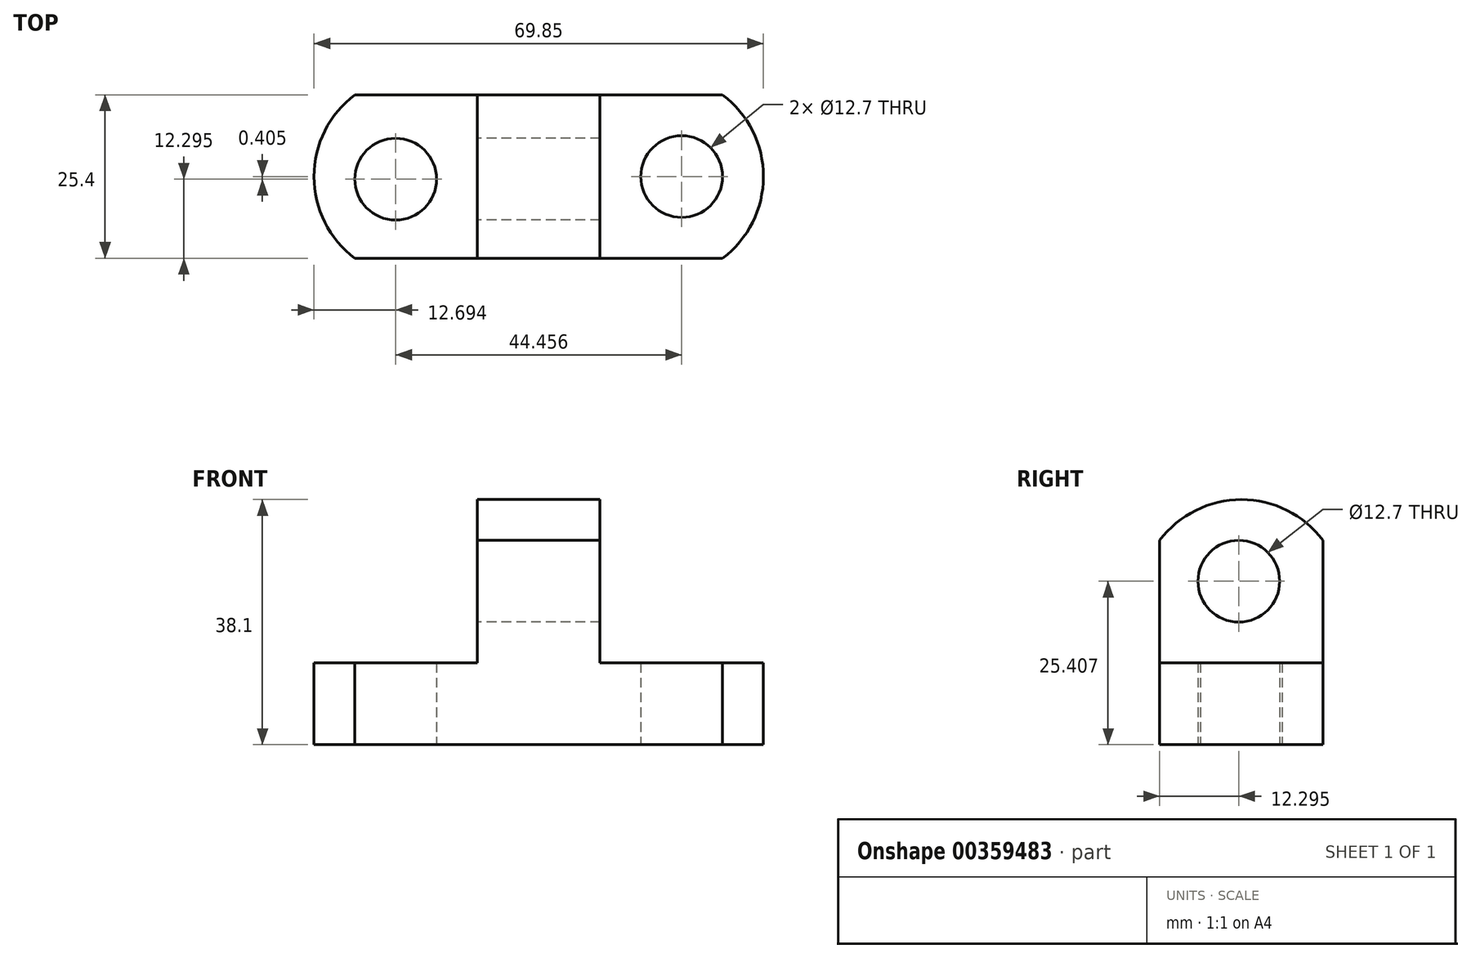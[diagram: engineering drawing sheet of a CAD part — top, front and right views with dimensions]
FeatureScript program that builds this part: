
annotation { "Feature Type Name" : "Feature", "Feature Type Description" : "" }
export const myFeature = defineFeature(function(context is Context, id is Id, definition is map)
    precondition{}
    {
        {
            var Q0;
            Q0=qCreatedBy(makeId("Front.planeOp"),FACE);
            var sketch = newSketch(context, id + "F0", { "sketchPlane" : qUnion([Q0])});
            skLineSegment(sketch, "E0", {"start": v(0, 38.1) * mm, "end": v(0, 0) * mm});
            skLineSegment(sketch, "E1", {"start": v(0, 0) * mm, "end": v(69.85, 0) * mm});
            skLineSegment(sketch, "E2", {"start": v(69.85, 0) * mm, "end": v(69.85, 38.1) * mm});
            skLineSegment(sketch, "E3", {"start": v(69.85, 38.1) * mm, "end": v(0, 38.1) * mm});
            skSolve(sketch);
        }
        {
            var Q0;
            Q0 = qSketchRegion(id + "F0", true);
            extrude(context, id + "F1", {"entities" : qUnion([Q0]), "oppositeDirection" : true, "depth" : 25.4 * mm});
        }
        {
            var Q0;
            Q0=qCreatedBy(makeId("Front.planeOp"),FACE);
            var sketch = newSketch(context, id + "F2", { "sketchPlane" : qUnion([Q0])});
            skLineSegment(sketch, "E4", {"start": v(44.45, 38.1) * mm, "end": v(44.45, 12.7) * mm});
            skLineSegment(sketch, "E5", {"start": v(44.45, 12.7) * mm, "end": v(69.85, 12.7) * mm});
            skLineSegment(sketch, "E6", {"start": v(69.85, 12.7) * mm, "end": v(69.85, 38.1) * mm});
            skLineSegment(sketch, "E7", {"start": v(69.85, 38.1) * mm, "end": v(44.45, 38.1) * mm});
            skSolve(sketch);
        }
        {
            var Q0;
            Q0 = qSketchRegion(id + "F2", true);
            extrude(context, id + "F3", {"entities" : qUnion([Q0]), "operationType" : NewBodyOperationType.REMOVE, "oppositeDirection" : true, "depth" : 25.4 * mm});
        }
        {
            var Q0;
            Q0=qCreatedBy(makeId("Front.planeOp"),FACE);
            var sketch = newSketch(context, id + "F4", { "sketchPlane" : qUnion([Q0])});
            skLineSegment(sketch, "E8", {"start": v(25.4, 38.1) * mm, "end": v(25.4, 12.7) * mm});
            skLineSegment(sketch, "E9", {"start": v(25.4, 12.7) * mm, "end": v(0, 12.7) * mm});
            skLineSegment(sketch, "E10", {"start": v(0, 12.7) * mm, "end": v(0, 38.1) * mm});
            skLineSegment(sketch, "E11", {"start": v(0, 38.1) * mm, "end": v(25.4, 38.1) * mm});
            skSolve(sketch);
        }
        {
            var Q0;
            Q0 = qSketchRegion(id + "F4", true);
            extrude(context, id + "F5", {"entities" : qUnion([Q0]), "operationType" : NewBodyOperationType.REMOVE, "oppositeDirection" : true, "depth" : 25.4 * mm});
        }
        {
            var Q0;
            Q0=qCreatedBy(makeId("Top.planeOp"),FACE);
            var sketch = newSketch(context, id + "F6", { "sketchPlane" : qUnion([Q0])});
            skArc(sketch, "E12", {"start": v(63.5, 0) * mm, "mid": v(69.85, 12.7) * mm, "end": v(63.5, 25.4) * mm});
            skLineSegment(sketch, "E13", {"start": v(63.5, 25.4) * mm, "end": v(69.85, 25.4) * mm});
            skLineSegment(sketch, "E14", {"start": v(69.85, 25.4) * mm, "end": v(69.85, 0) * mm});
            skLineSegment(sketch, "E15", {"start": v(69.85, 0) * mm, "end": v(63.5, 0) * mm});
            skSolve(sketch);
        }
        {
            var Q0;
            Q0 = qSketchRegion(id + "F6", true);
            extrude(context, id + "F7", {"entities" : qUnion([Q0]), "operationType" : NewBodyOperationType.REMOVE, "depth" : 25.4 * mm});
        }
        {
            var Q0;
            Q0=qCreatedBy(makeId("Top.planeOp"),FACE);
            var sketch = newSketch(context, id + "F8", { "sketchPlane" : qUnion([Q0])});
            skArc(sketch, "E16", {"start": v(6.35, 25.4) * mm, "mid": v(0, 12.7) * mm, "end": v(6.35, 0) * mm});
            skLineSegment(sketch, "E17", {"start": v(6.35, 25.4) * mm, "end": v(0, 25.4) * mm});
            skLineSegment(sketch, "E18", {"start": v(0, 25.4) * mm, "end": v(0, 0) * mm});
            skLineSegment(sketch, "E19", {"start": v(0, 0) * mm, "end": v(6.35, 0) * mm});
            skSolve(sketch);
        }
        {
            var Q0;
            Q0 = qSketchRegion(id + "F8", true);
            extrude(context, id + "F9", {"entities" : qUnion([Q0]), "operationType" : NewBodyOperationType.REMOVE, "depth" : 25.4 * mm});
        }
        {
            var Q0;
            Q0=qCreatedBy(makeId("Right.planeOp"),FACE);
            var sketch = newSketch(context, id + "F10", { "sketchPlane" : qUnion([Q0])});
            skArc(sketch, "E20", {"start": v(25.4, 31.75) * mm, "mid": v(12.7, 38.1) * mm, "end": v(0, 31.75) * mm});
            skLineSegment(sketch, "E21", {"start": v(0, 31.75) * mm, "end": v(0, 38.1) * mm});
            skLineSegment(sketch, "E22", {"start": v(0, 38.1) * mm, "end": v(25.4, 38.1) * mm});
            skLineSegment(sketch, "E23", {"start": v(25.4, 38.1) * mm, "end": v(25.4, 31.75) * mm});
            skSolve(sketch);
        }
        {
            var Q0;
            Q0 = qSketchRegion(id + "F10", true);
            extrude(context, id + "F11", {"entities" : qUnion([Q0]), "operationType" : NewBodyOperationType.REMOVE, "depth" : 50.8 * mm});
        }
        {
            var Q0;
            Q0=qCreatedBy(makeId("Top.planeOp"),FACE);
            var sketch = newSketch(context, id + "F12", { "sketchPlane" : qUnion([Q0])});
            skCircle(sketch, "E24", {"center": v(12.7, 12.3) * mm, "radius": 6.35 * mm});
            skCircle(sketch, "E25", {"center": v(57.15, 12.7) * mm, "radius": 6.35 * mm});
            skSolve(sketch);
        }
        {
            var Q0;
            Q0 = qSketchRegion(id + "F12", true);
            extrude(context, id + "F13", {"entities" : qUnion([Q0]), "operationType" : NewBodyOperationType.REMOVE, "depth" : 25.4 * mm});
        }
        {
            var Q0;
            Q0=qCreatedBy(makeId("Right.planeOp"),FACE);
            var sketch = newSketch(context, id + "F14", { "sketchPlane" : qUnion([Q0])});
            skCircle(sketch, "E26", {"center": v(12.3, 25.4) * mm, "radius": 6.35 * mm});
            skSolve(sketch);
        }
        {
            var Q0;
            Q0 = qSketchRegion(id + "F14", true);
            extrude(context, id + "F15", {"entities" : qUnion([Q0]), "operationType" : NewBodyOperationType.REMOVE, "depth" : 50.8 * mm});
        }
    });
